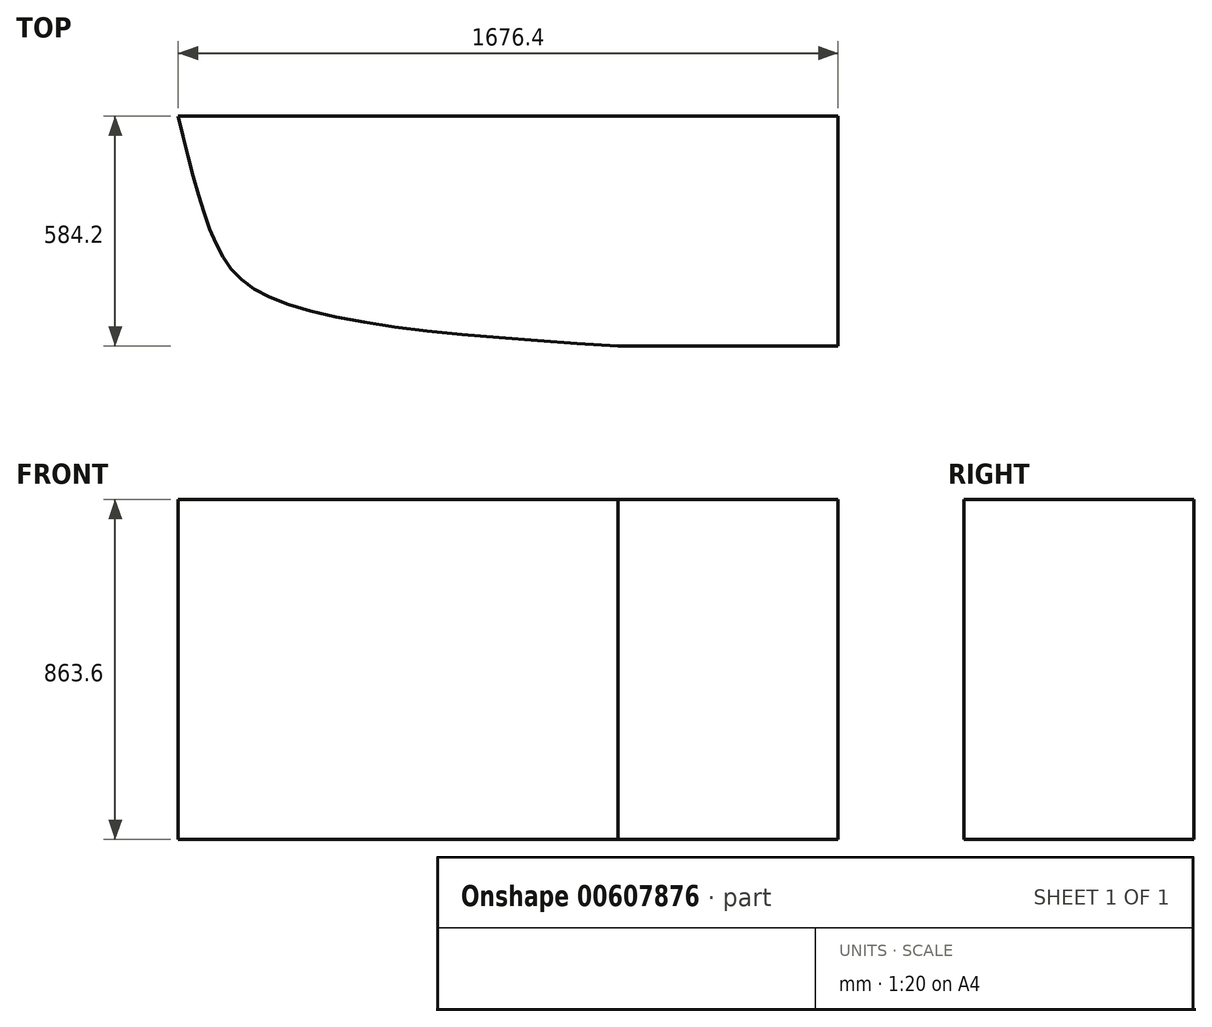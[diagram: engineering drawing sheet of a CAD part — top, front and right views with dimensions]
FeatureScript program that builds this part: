
annotation { "Feature Type Name" : "Feature", "Feature Type Description" : "" }
export const myFeature = defineFeature(function(context is Context, id is Id, definition is map)
    precondition{}
    {
        {
            var Q0;
            Q0=qCreatedBy(makeId("Top.planeOp"),FACE);
            var sketch = newSketch(context, id + "F0", { "sketchPlane" : qUnion([Q0])});
            skLineSegment(sketch, "E0.bottom", {"start": v(0, 0) * mm, "end": v(-1676.4, 0) * mm});
            skLineSegment(sketch, "E0.top", {"start": v(0, -584.2) * mm, "end": v(-558.8, -584.2) * mm});
            skLineSegment(sketch, "E0.left", {"start": v(0, 0) * mm, "end": v(0, -584.2) * mm});
            skFitSpline(sketch, "E1", {"points": [v(-1676.4, 0) * mm, v(-1585.9, -312.3) * mm, v(-1448.47, -458.32) * mm, v(-558.8, -584.2) * mm], "startDerivative": vector(293.05, -1209.04) * mm, "endDerivative": vector(2419.46, -148.7) * mm});
            skSolve(sketch);
        }
        {
            var Q0;
            Q0=makeQuery(id+"F0.imprint","IMPRINT",FACE,{"disambiguationData":[TD([[makeQuery(id+"F0.imprint","IMPRINT",EDGE,{"derivedFrom":sQuery(id+"F0.wireOp",EDGE,"E0.bottom")}),1.0]])]});
            extrude(context, id + "F1", {"entities" : qUnion([Q0]), "depth" : 863.6 * mm, "offsetDistance" : 25.4 * mm});
        }
    });
